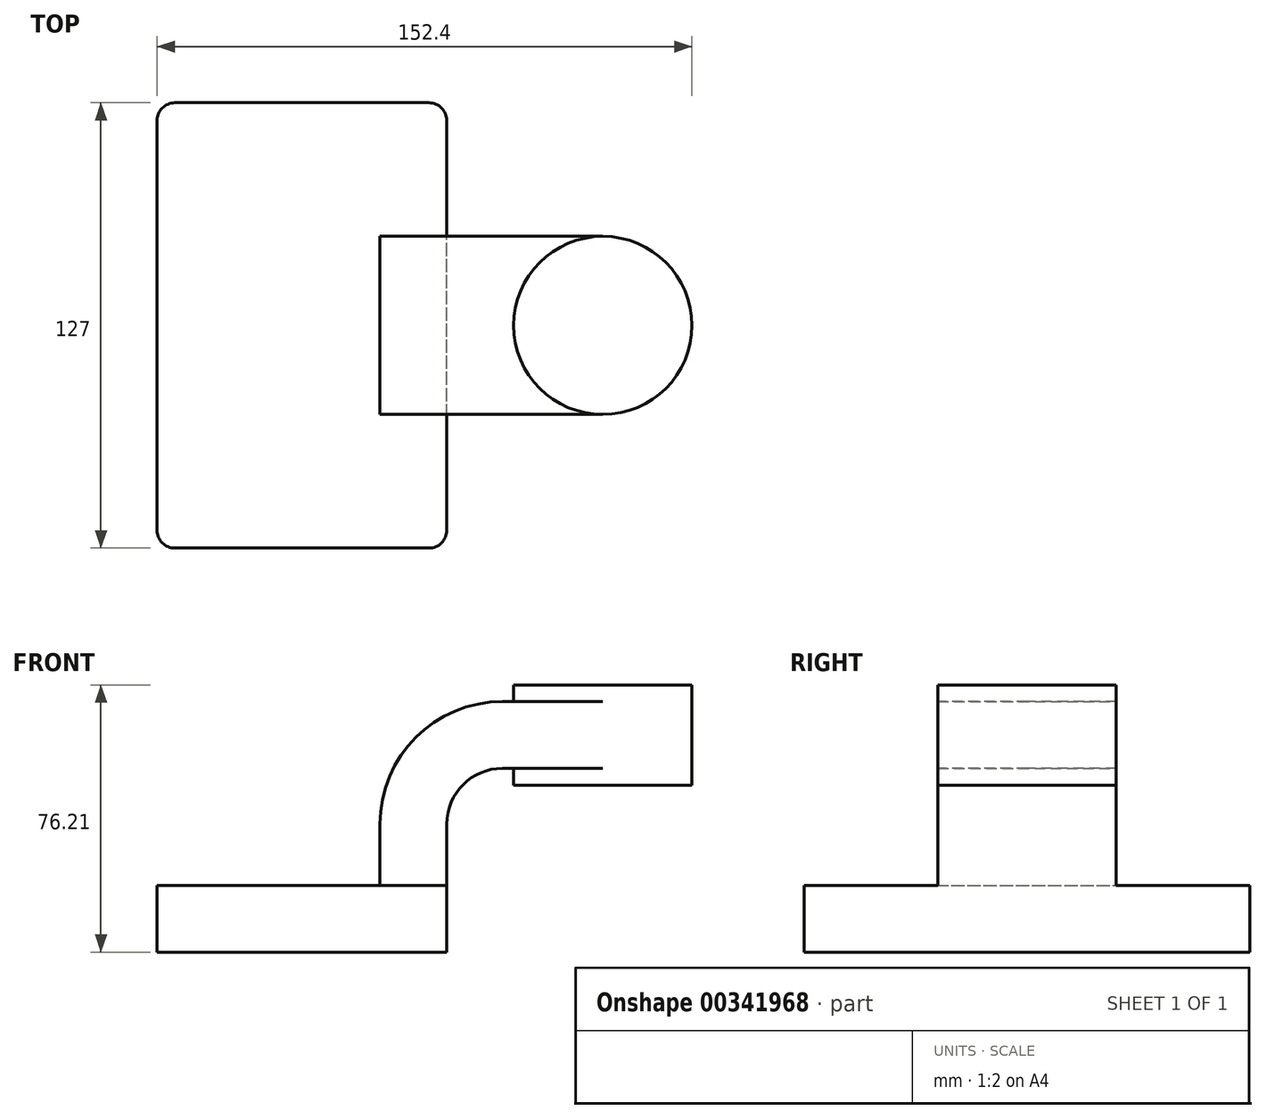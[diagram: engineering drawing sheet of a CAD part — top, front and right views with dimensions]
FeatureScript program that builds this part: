
annotation { "Feature Type Name" : "Feature", "Feature Type Description" : "" }
export const myFeature = defineFeature(function(context is Context, id is Id, definition is map)
    precondition{}
    {
        {
            var Q0;
            Q0=qCreatedBy(makeId("Front.planeOp"),FACE);
            var sketch = newSketch(context, id + "F0", { "sketchPlane" : qUnion([Q0])});
            skLineSegment(sketch, "E0.bottom", {"start": v(41.27, 9.53) * mm, "end": v(-41.28, 9.53) * mm});
            skLineSegment(sketch, "E0.top", {"start": v(41.28, -9.52) * mm, "end": v(-41.27, -9.52) * mm});
            skLineSegment(sketch, "E0.left", {"start": v(41.28, 9.53) * mm, "end": v(41.28, -9.52) * mm});
            skLineSegment(sketch, "E0.right", {"start": v(-41.28, 9.53) * mm, "end": v(-41.27, -9.52) * mm});
            skPoint(sketch, "E0.middle", {"position": v(0, 0) * mm});
            skLineSegment(sketch, "E1.bottom", {"start": v(111.12, 66.68) * mm, "end": v(60.32, 66.68) * mm});
            skLineSegment(sketch, "E1.top", {"start": v(111.12, 38.1) * mm, "end": v(60.32, 38.1) * mm});
            skLineSegment(sketch, "E1.left", {"start": v(111.12, 66.68) * mm, "end": v(111.12, 38.1) * mm});
            skLineSegment(sketch, "E1.right", {"start": v(60.32, 66.68) * mm, "end": v(60.32, 38.1) * mm});
            skPoint(sketch, "E1.middle", {"position": v(85.72, 42.88) * mm});
            skLineSegment(sketch, "E2", {"start": v(41.27, 9.53) * mm, "end": v(41.27, 27) * mm});
            skArc(sketch, "E3", {"start": v(41.27, 27) * mm, "mid": v(45.92, 38.23) * mm, "end": v(57.15, 42.88) * mm});
            skLineSegment(sketch, "E4", {"start": v(57.15, 42.88) * mm, "end": v(85.72, 42.88) * mm});
            skLineSegment(sketch, "E5", {"start": v(85.72, 38.1) * mm, "end": v(85.72, 66.68) * mm});
            skLineSegment(sketch, "E6.0", {"start": v(57.15, 61.93) * mm, "end": v(85.72, 61.93) * mm});
            skArc(sketch, "E6.1", {"start": v(22.22, 27) * mm, "mid": v(32.45, 51.7) * mm, "end": v(57.15, 61.93) * mm});
            skLineSegment(sketch, "E6.2", {"start": v(22.22, 9.53) * mm, "end": v(22.22, 27) * mm});
            skPoint(sketch, "E7.orphan", {"position": v(85.72, 66.68) * mm});
            skFitSpline(sketch, "E8", {"points": [v(57.15, 61.93) * mm, v(-23.17, 50.9) * mm, v(-41.28, 9.52) * mm], "startDerivative": vector(-170.25, 0) * mm, "endDerivative": vector(-14.24, -106.59) * mm});
            skSolve(sketch);
        }
        {
            var Q0;
            Q0=makeQuery(id+"F0.imprint","IMPRINT",FACE,{"disambiguationData":[TD([[makeQuery(id+"F0.imprint","IMPRINT",EDGE,{"derivedFrom":sQuery(id+"F0.wireOp",EDGE,"E0.top")}),-1.0]])]});
            extrude(context, id + "F1", {"entities" : qUnion([Q0]), "endBound" : BoundingType.SYMMETRIC, "depth" : 127 * mm});
        }
        {
            var Q0;
            {var subQ1=sQuery(id+"F0.wireOp",EDGE,"E2");Q0=makeQuery(id+"F0.imprint","IMPRINT",FACE,{"disambiguationData":[TD([[makeQuery(id+"F0.imprint","IMPRINT",EDGE,{"derivedFrom":subQ1}),1.0]])]});}
            var Q1;
            {var subQ0=sQuery(id+"F0.wireOp",EDGE,"E6.0");var subQ1=sQuery(id+"F0.wireOp",EDGE,"E1.right");var subQ2=makeQuery(id+"F0.imprint","INTERSECT",VERTEX,{"derivedFrom":[subQ1,subQ0]});Q1=makeQuery(id+"F0.imprint","IMPRINT",FACE,{"disambiguationData":[TD([[makeQuery(id+"F0.imprint","IMPRINT",EDGE,{"disambiguationData":[TD([[subQ2,-1.0]])],"derivedFrom":subQ1}),1.0]])]});}
            extrude(context, id + "F2", {"entities" : qUnion([Q0, Q1]), "operationType" : NewBodyOperationType.ADD, "endBound" : BoundingType.SYMMETRIC, "depth" : 50.8 * mm});
        }
        {
            var Q0;
            {var subQ0=sQuery(id+"F0.wireOp",EDGE,"E1.left");Q0=makeQuery(id+"F0.imprint","IMPRINT",FACE,{"disambiguationData":[TD([[makeQuery(id+"F0.imprint","IMPRINT",EDGE,{"derivedFrom":subQ0}),-1.0]])]});}
            var Q1;
            Q1=sQuery(id+"F0.wireOp",EDGE,"E5");
            revolve(context, id + "F3", {"operationType" : NewBodyOperationType.ADD, "entities" : qUnion([Q0]), "axis" : qUnion([Q1]), "revolveType" : RevolveType.FULL});
        }
        {
            var Q0;
            Q0=makeQuery(id+"F0.imprint","IMPRINT",FACE,{"disambiguationData":[TD([[makeQuery(id+"F0.imprint","IMPRINT",EDGE,{"derivedFrom":sQuery(id+"F0.wireOp",EDGE,"E6.1")}),1.0]])]});
            extrude(context, id + "F4", {"entities" : qUnion([Q0]), "operationType" : NewBodyOperationType.ADD, "endBound" : BoundingType.SYMMETRIC, "depth" : 15.88 * mm});
        }
        {
            var Q0;
            Q0=makeQuery(id+"F1.opExtrude","CAP_EDGE",EDGE,{"disambiguationData":[OSD([sQuery(id+"F0.wireOp",EDGE,"E0.right")])],"isStart":false});
            var Q1;
            Q1=makeQuery(id+"F1.opExtrude","CAP_EDGE",EDGE,{"disambiguationData":[OSD([sQuery(id+"F0.wireOp",EDGE,"E0.left")])],"isStart":false});
            var Q2;
            Q2=makeQuery(id+"F1.opExtrude","CAP_EDGE",EDGE,{"disambiguationData":[OSD([sQuery(id+"F0.wireOp",EDGE,"E0.left")])],"isStart":true});
            var Q3;
            Q3=makeQuery(id+"F1.opExtrude","CAP_EDGE",EDGE,{"disambiguationData":[OSD([sQuery(id+"F0.wireOp",EDGE,"E0.right")])],"isStart":true});
            fillet(context, id + "F5", {"entities" : qUnion([Q0, Q1, Q2, Q3]), "radius" : 5.08 * mm, "tangentPropagation" : true, "allowEdgeOverflow" : false});
        }
    });
